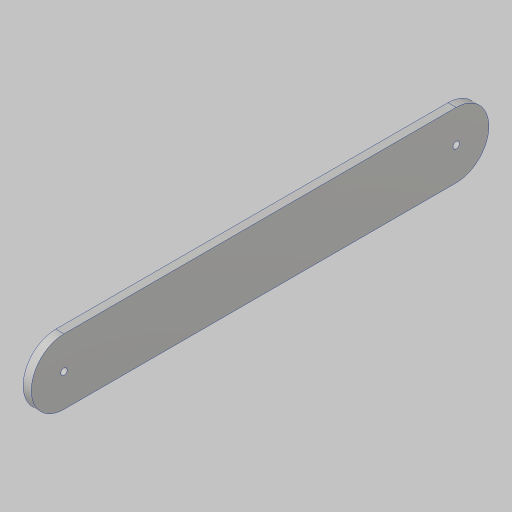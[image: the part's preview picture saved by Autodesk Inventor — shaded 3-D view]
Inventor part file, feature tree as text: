
AUTODESK INVENTOR PART (.ipt)
format: ipt  version: 2023.5 (Build 275446000, 446)  size: 89,088 bytes
history: native  units: in
note: dims shown in document units (in); Inventor stores cm internally (conversion verified against a paired STEP export)
features: sketch x1, extrude x1, hole x1
ambient origin geometry x8: Origin, YZ Plane, XZ Plane, XY Plane, X Axis, Y Axis, Z Axis, Center Point
bodies: Solid1 (feature_tree)
feature tree (3):
  sketch  "Sketch1"  dims[d0=2.0in d1=12.0in d2=0.25in d3=0.0in d4=0.201in d5=0.75in d6=0.385in d7=0.25in d8=0.5635in d9=1.0in d10=0.8108in]
  extrude  "Extrusion1"  Depth=1.0in
  hole  "Hole1"  [1 undecoded]
note: 1 required parameter value undecoded (feature->parameter linkage not recoverable at this tier; creation-order binding heuristic only, values carry confidence <= 0.55)
